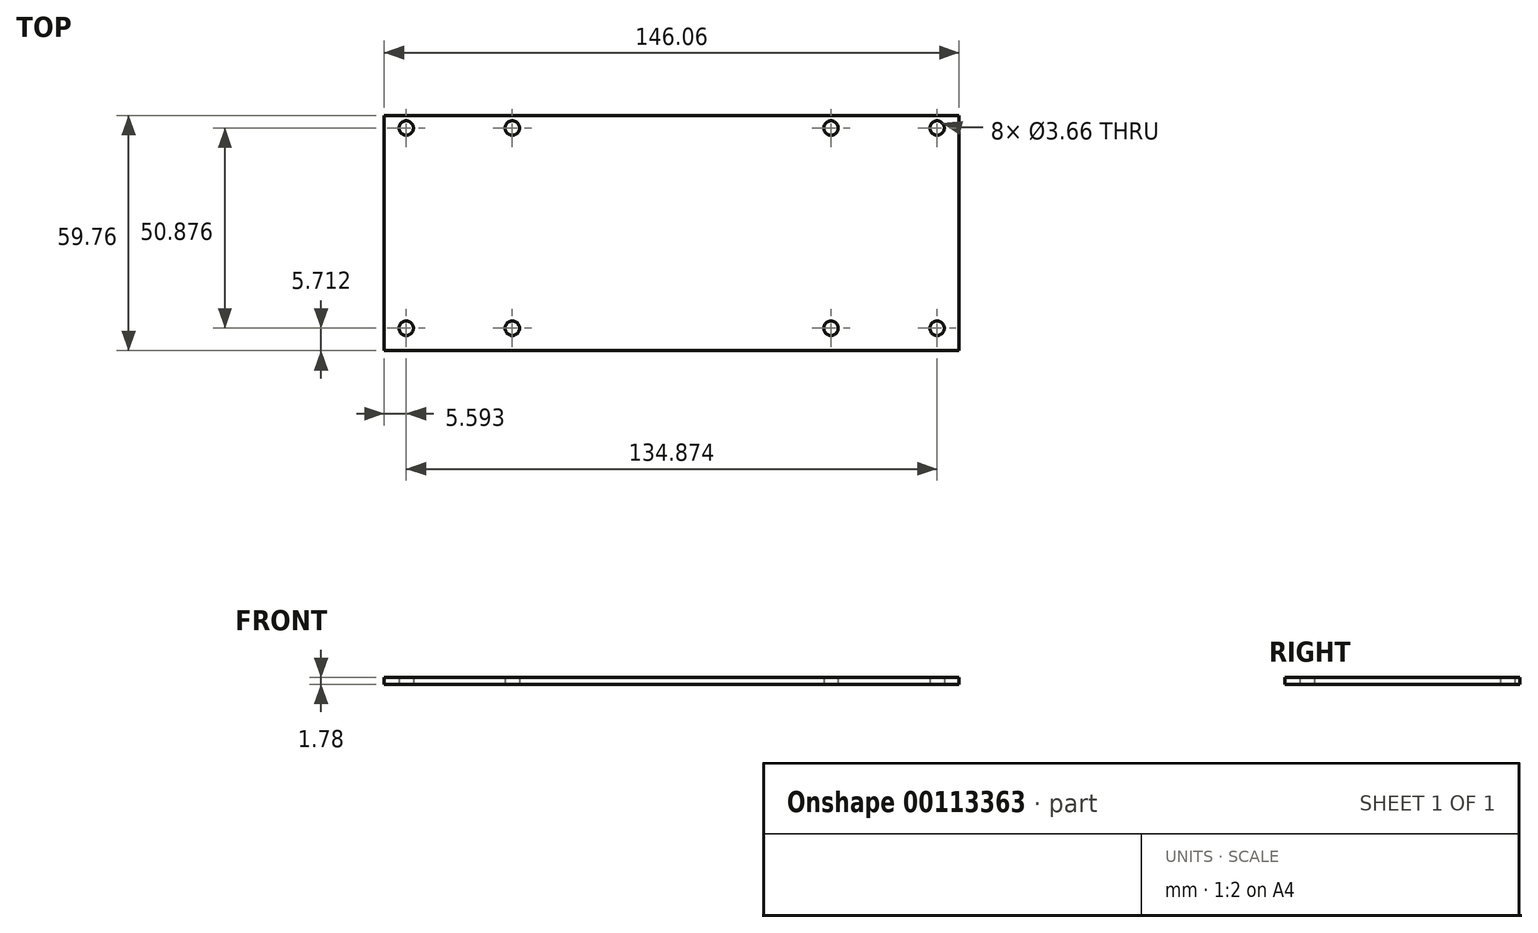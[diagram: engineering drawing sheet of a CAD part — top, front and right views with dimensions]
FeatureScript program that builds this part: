
annotation { "Feature Type Name" : "Feature", "Feature Type Description" : "" }
export const myFeature = defineFeature(function(context is Context, id is Id, definition is map)
    precondition{}
    {
        {
            var Q0;
            Q0=qCreatedBy(makeId("Top.planeOp"),FACE);
            var sketch = newSketch(context, id + "F0", { "sketchPlane" : qUnion([Q0])});
            skLineSegment(sketch, "E0.bottom", {"start": v(73.02, 29.88) * mm, "end": v(-73.03, 29.88) * mm});
            skLineSegment(sketch, "E0.top", {"start": v(73.03, -29.88) * mm, "end": v(-73.02, -29.88) * mm});
            skLineSegment(sketch, "E0.left", {"start": v(73.02, 29.88) * mm, "end": v(73.03, -29.88) * mm});
            skLineSegment(sketch, "E0.right", {"start": v(-73.03, 29.88) * mm, "end": v(-73.02, -29.88) * mm});
            skPoint(sketch, "E0.middle", {"position": v(0, 0) * mm});
            skCircle(sketch, "E1", {"center": v(-67.44, 26.7) * mm, "radius": 1.83 * mm});
            skCircle(sketch, "E2", {"center": v(-40.49, 26.7) * mm, "radius": 1.83 * mm});
            skCircle(sketch, "E3", {"center": v(-67.44, -24.17) * mm, "radius": 1.83 * mm});
            skCircle(sketch, "E4", {"center": v(-40.49, -24.17) * mm, "radius": 1.83 * mm});
            skCircle(sketch, "E5", {"center": v(67.44, 26.7) * mm, "radius": 1.83 * mm});
            skCircle(sketch, "E6", {"center": v(40.49, 26.7) * mm, "radius": 1.83 * mm});
            skCircle(sketch, "E7", {"center": v(67.44, -24.17) * mm, "radius": 1.83 * mm});
            skCircle(sketch, "E8", {"center": v(40.49, -24.17) * mm, "radius": 1.83 * mm});
            skSolve(sketch);
        }
        {
            var Q0;
            Q0=makeQuery(id+"F0.imprint","IMPRINT",FACE,{"disambiguationData":[TD([[makeQuery(id+"F0.imprint","IMPRINT",EDGE,{"derivedFrom":sQuery(id+"F0.wireOp",EDGE,"E0.bottom")}),1.0]])]});
            extrude(context, id + "F1", {"entities" : qUnion([Q0]), "depth" : 1.78 * mm, "offsetDistance" : 25.4 * mm});
        }
    });
